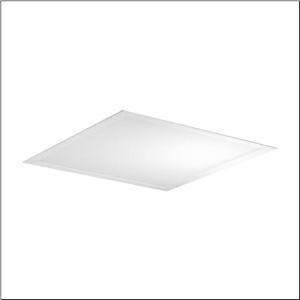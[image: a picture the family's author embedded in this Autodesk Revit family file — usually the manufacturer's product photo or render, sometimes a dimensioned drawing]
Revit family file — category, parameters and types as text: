
# Revit family: apollon_r__21_square_51mq11wd2414_f5b9
name_source: partatom
category: Lighting Fixtures
units: mm (PartAtom-declared; Revit-internal decimal feet)

## family parameters
Cut with Voids When Loaded = No
Host = Face
Light Source = No
Part Type = Normal
Room Calculation Point = No
Round Connector Dimension = Use Diameter
Shared = No

## types (1)
- Apollon® 21 square (1 x LED, 4200 lm, 24.7 W, 4000K)
    Apparent Load = 25 VA
    CIE Flux Codes = 60 87 97 100 100
    Color Rendering = 80
    Color Temperature = 4000K
    Default Elevation = 1800 mm
    Description = Apollon® 21 square, office luminaire, primary optical cover: micro prismatic cover, of PMMA, CAT 2 (L<= 3000cd/m²), light emission: direct distribution, primary light characteristic: symmetric, installation type: lay-in mounting, LED, rated luminous flux: 4.200lm, luminous efficacy: 170lm/W, light colour: 840, colour temperature: 4000K, with terminal, 5-pole, mains connection: 220..240V, AC/DC, 0/50..60Hz, rated input power: 24.7W, housing, of aluminium, coated, traffic white (RAL 9016), module: M625, length: 620mm, width: 620mm, height: 30mm, housing upper side, of sheet steel, galvanised, protection rating (complete): IP20, protection rating (lamp compartment, on room side): IP50, insulation class (complete): insulation class II (safety insulation), certification: CE, ENEC, impact resistance: IK03, permissible operating ambient temperature: -20..+45°C, permissible storage temperature: -40..+80°C, packaging unit: 1 piece
    Height = 0 mm  [stored 0 ft]
    Lamp = 1 x LED
    Lamp Light Flux = 4200 lm
    Lamp Power = 24.7 W
    Lamp count = 1
    Length = 620 mm
    Luminous efficacy = 170 lm/W
    Manufacturer = Siteco
    ModVariant = No
    Model = 51MQ11WD2414
    Mounting Place = Ceiling
    Mounting Type = Recessed
    Number of Poles = 1
    OnlyDefault = Yes
    Power Factor = 1
    Product Name = Apollon® 21 square
    Product group = office luminaire | ceiling recessed
    ProductGroupID = 401
    Protection Class = Protection class II
    Protection Degree = IP 20
    RLX_Detail_Level = 1
    RLX_Emergency_Light_Flux = 0 lm
    RLX_Emergency_Type = 0
    RLX_Emergency_Type_DB = No
    RlxData = <blob elided: 12961 chars, md5=b5f163b9>
    Socket = socket
    Standby Power = 0 W
    System Light Flux = 4200 lm
    System Power = 25 W
    Type Comments = Product without accessories
    Type Image = l_1291054.jpg
    URL = http://relux.com
    VarID = ---
    Voltage = 0 V
    Weight = 0.00 kg
    Width = 620 mm

note: [stored X ft] marks values corroborated as IEEE doubles in the binary element streams (Revit-internal decimal feet)

## geometry (parser evidence)
native form markers: Sweep x10
no freeform markers — native parametric forms only
